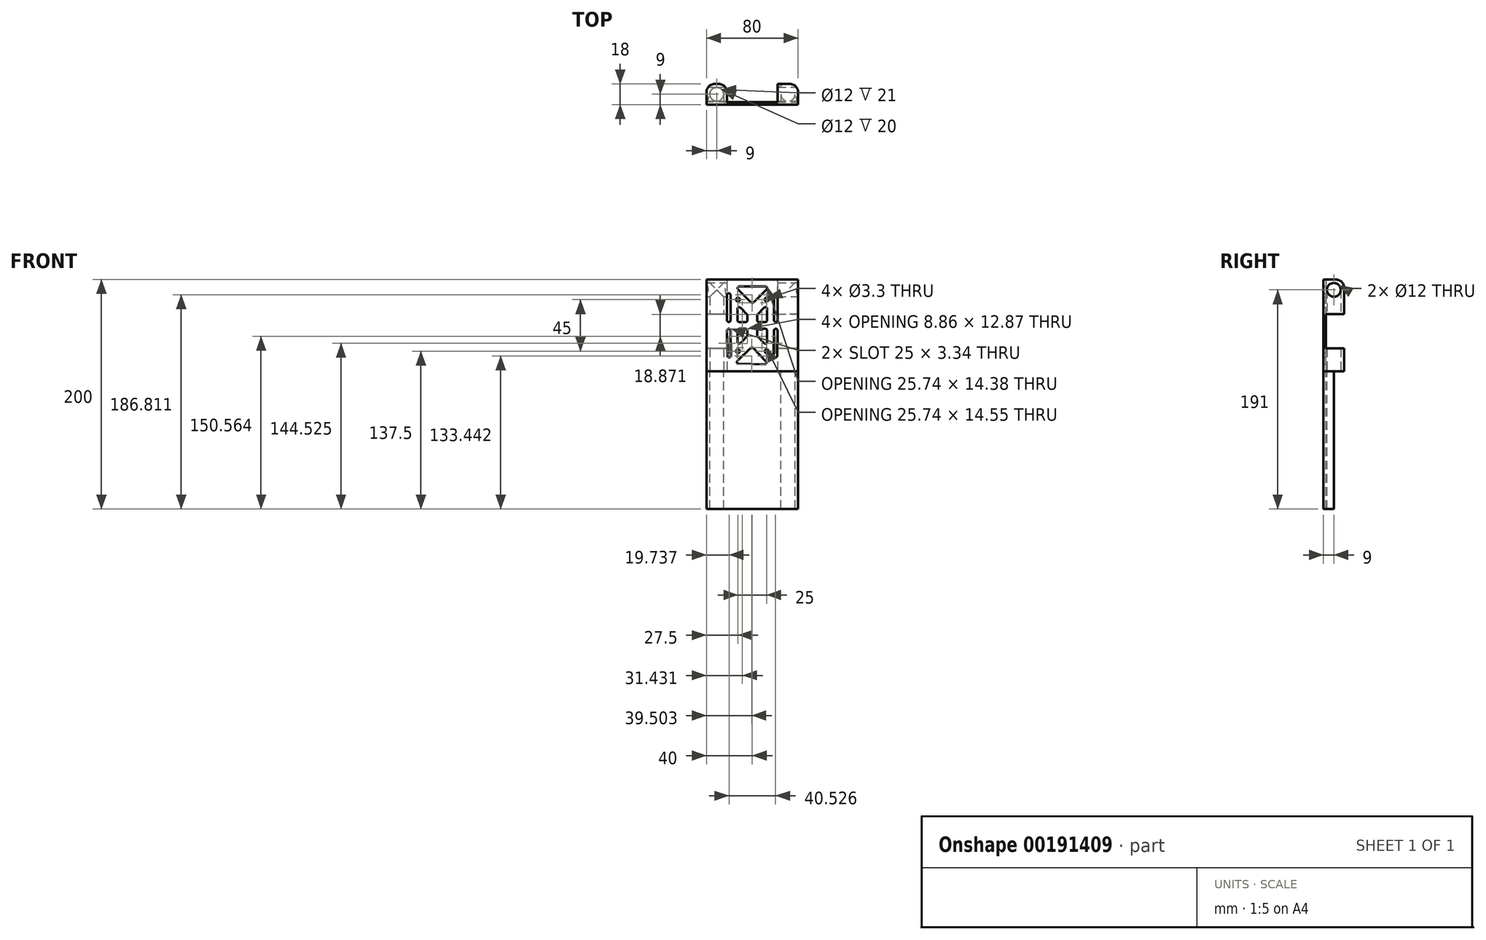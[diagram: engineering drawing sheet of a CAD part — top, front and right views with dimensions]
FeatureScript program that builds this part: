
annotation { "Feature Type Name" : "Feature", "Feature Type Description" : "" }
export const myFeature = defineFeature(function(context is Context, id is Id, definition is map)
    precondition{}
    {
        {
            var Q0;
            Q0=qCreatedBy(makeId("Top.planeOp"),FACE);
            var sketch = newSketch(context, id + "F0", { "sketchPlane" : qUnion([Q0])});
            skLineSegment(sketch, "E0.bottom", {"start": v(-40, 9) * mm, "end": v(40, 9) * mm});
            skLineSegment(sketch, "E0.top", {"start": v(-40, -9) * mm, "end": v(40, -9) * mm});
            skLineSegment(sketch, "E0.left", {"start": v(-40, 9) * mm, "end": v(-40, -9) * mm});
            skLineSegment(sketch, "E0.right", {"start": v(40, 9) * mm, "end": v(40, -9) * mm});
            skSolve(sketch);
        }
        {
            var Q0;
            Q0=qCreatedBy(makeId("Top.planeOp"),FACE);
            var sketch = newSketch(context, id + "F1", { "sketchPlane" : qUnion([Q0])});
            skCircle(sketch, "E1", {"center": v(-31, 0) * mm, "radius": 6 * mm});
            skCircle(sketch, "E2.MirrorC", {"center": v(31, 0) * mm, "radius": 6 * mm});
            skSolve(sketch);
        }
        {
            var Q0;
            Q0=makeQuery(id+"F0.imprint","IMPRINT",FACE,{"disambiguationData":[TD([[makeQuery(id+"F0.imprint","IMPRINT",EDGE,{"derivedFrom":sQuery(id+"F0.wireOp",EDGE,"E0.bottom")}),-1.0]])]});
            extrude(context, id + "F2", {"entities" : qUnion([Q0]), "depth" : 80 * mm});
        }
        {
            var Q0;
            Q0=makeQuery(id+"F2.opExtrude","SWEPT_FACE",FACE,{"disambiguationData":[OSD([sQuery(id+"F0.wireOp",EDGE,"E0.right")])]});
            var sketch = newSketch(context, id + "F3", { "sketchPlane" : qUnion([Q0])});
            skCircle(sketch, "E3", {"center": v(0, 71) * mm, "radius": 6 * mm});
            skSolve(sketch);
        }
        {
            var Q0;
            Q0 = qSketchRegion(id + "F3", true);
            extrude(context, id + "F4", {"entities" : qUnion([Q0]), "operationType" : NewBodyOperationType.REMOVE, "endBound" : BoundingType.UP_TO_NEXT, "oppositeDirection" : true, "depth" : 25 * mm});
        }
        {
            var Q0;
            Q0=makeQuery(id+"F1.imprint","IMPRINT",FACE,{"disambiguationData":[TD([[makeQuery(id+"F1.imprint","IMPRINT",EDGE,{"derivedFrom":sQuery(id+"F1.wireOp",EDGE,"E2.MirrorC")}),-1.0]])]});
            var Q1;
            Q1=makeQuery(id+"F1.imprint","IMPRINT",FACE,{"disambiguationData":[TD([[makeQuery(id+"F1.imprint","IMPRINT",EDGE,{"derivedFrom":sQuery(id+"F1.wireOp",EDGE,"E1")}),1.0]])]});
            extrude(context, id + "F5", {"entities" : qUnion([Q0, Q1]), "operationType" : NewBodyOperationType.REMOVE, "endBound" : BoundingType.UP_TO_NEXT, "depth" : 63.6 * mm});
        }
        {
            var Q0;
            Q0=makeQuery(id+"F2.opExtrude","SWEPT_FACE",FACE,{"disambiguationData":[OSD([sQuery(id+"F0.wireOp",EDGE,"E0.bottom")])]});
            var sketch = newSketch(context, id + "F6", { "sketchPlane" : qUnion([Q0])});
            skLineSegment(sketch, "E4.0", {"start": v(-22, 62) * mm, "end": v(-22, 0) * mm});
            skLineSegment(sketch, "E5", {"start": v(22, 0) * mm, "end": v(-22, 0) * mm});
            skLineSegment(sketch, "E6", {"start": v(-22, 62) * mm, "end": v(-22, 80) * mm});
            skLineSegment(sketch, "E7", {"start": v(-22, 80) * mm, "end": v(22, 80) * mm});
            skLineSegment(sketch, "E8", {"start": v(22, 80) * mm, "end": v(22, 0) * mm});
            skLineSegment(sketch, "E9.bottom", {"start": v(-22, 20) * mm, "end": v(-40, 20) * mm});
            skLineSegment(sketch, "E9.top", {"start": v(-22, 50) * mm, "end": v(-40, 50) * mm});
            skLineSegment(sketch, "E9.left", {"start": v(-22, 20) * mm, "end": v(-22, 50) * mm});
            skLineSegment(sketch, "E9.right", {"start": v(-40, 20) * mm, "end": v(-40, 50) * mm});
            skLineSegment(sketch, "E10.MirrorCS", {"start": v(40, 20) * mm, "end": v(40, 50) * mm});
            skLineSegment(sketch, "E11.MirrorCS", {"start": v(22, 50) * mm, "end": v(40, 50) * mm});
            skLineSegment(sketch, "E12.MirrorCS", {"start": v(22, 20) * mm, "end": v(22, 50) * mm});
            skLineSegment(sketch, "E13.MirrorCS", {"start": v(22, 20) * mm, "end": v(40, 20) * mm});
            skSolve(sketch);
        }
        {
            var Q0;
            Q0 = qSketchRegion(id + "F6", true);
            extrude(context, id + "F7", {"entities" : qUnion([Q0]), "operationType" : NewBodyOperationType.REMOVE, "oppositeDirection" : true, "depth" : 16 * mm});
        }
        {
            var Q0;
            Q0=makeQuery(id+"F2.opExtrude","SWEPT_FACE",FACE,{"disambiguationData":[OSD([sQuery(id+"F0.wireOp",EDGE,"E0.top")])]});
            cPlane(context, id + "F8", {"entities" : qUnion([Q0]), "cplaneType" : CPlaneType.OFFSET, "offset" : 0 * mm, "width" : 150 * mm, "height" : 150 * mm});
        }
        {
            var Q0;
            Q0=qCreatedBy(id+"F8.planeOp",FACE);
            var sketch = newSketch(context, id + "F9", { "sketchPlane" : qUnion([Q0])});
            skPoint(sketch, "E14", {"position": v(-12.5, 62.5) * mm});
            skPoint(sketch, "E15.MirrorP", {"position": v(12.5, 62.5) * mm});
            skPoint(sketch, "E16", {"position": v(-12.5, 17.5) * mm});
            skPoint(sketch, "E17.MirrorP", {"position": v(12.5, 17.5) * mm});
            skSolve(sketch);
        }
        {
            var Q0;
            Q0=sQuery(id+"F9.wireOp",VERTEX,"E15.MirrorP");
            var Q1;
            Q1=sQuery(id+"F9.wireOp",VERTEX,"E17.MirrorP");
            var Q2;
            Q2=sQuery(id+"F9.wireOp",VERTEX,"E16");
            var Q3;
            Q3=sQuery(id+"F9.wireOp",VERTEX,"E14");
            var Q4;
            Q4=makeQuery(id+"F2.opExtrude","SWEPT_BODY",BODY,{"disambiguationData":[OSD([sQuery(id+"F0.wireOp",EDGE,"E0.bottom"),sQuery(id+"F0.wireOp",EDGE,"E0.top"),sQuery(id+"F0.wireOp",EDGE,"E0.left"),sQuery(id+"F0.wireOp",EDGE,"E0.right")])]});
            hole(context, id + "F10", {"style" : HoleStyle.SIMPLE, "endStyle" : HoleEndStyle.THROUGH, "standardTappedOrClearance" : lookupTablePath({ "standard" : "ISO", "fit" : "Normal", "size" : "M3", "type" : "Clearance" }), "standardBlindInLast" : lookupTablePath({ "fit" : "Standard", "standard" : "ISO", "size" : "M3", "type" : "Clearance" }), "holeDiameter" : 3.3 * mm, "locations" : qUnion([Q0, Q1, Q2, Q3]), "scope" : qUnion([Q4]), "isTappedThrough" : true});
        }
        {
            var Q0;
            Q0=makeQuery(id+"F7.boolean.opBoolean","COPY",FACE,{"derivedFrom":makeQuery(id+"F7.opExtrude","CAP_FACE",FACE,{"disambiguationData":[OSD([sQuery(id+"F6.wireOp",EDGE,"E4.0"),sQuery(id+"F6.wireOp",EDGE,"E5"),sQuery(id+"F6.wireOp",EDGE,"E6"),sQuery(id+"F6.wireOp",EDGE,"E7"),sQuery(id+"F6.wireOp",EDGE,"E8")])],"isStart":false})});
            var sketch = newSketch(context, id + "F11", { "sketchPlane" : qUnion([Q0])});
            skLineSegment(sketch, "E18", {"start": v(-11.38, 74) * mm, "end": v(11.38, 74) * mm});
            skLineSegment(sketch, "E19", {"start": v(12.44, 71.44) * mm, "end": v(1.06, 60.06) * mm});
            skLineSegment(sketch, "E20", {"start": v(-1.06, 60.06) * mm, "end": v(-12.44, 71.44) * mm});
            skLineSegment(sketch, "E21.bottom", {"start": v(-20.5, 68) * mm, "end": v(-20.5, 68) * mm});
            skLineSegment(sketch, "E21.top", {"start": v(-20.5, 43) * mm, "end": v(-20.5, 43) * mm});
            skLineSegment(sketch, "E21.left", {"start": v(-22, 66.5) * mm, "end": v(-22, 44.5) * mm});
            skLineSegment(sketch, "E21.right", {"start": v(-19, 66.5) * mm, "end": v(-19, 44.5) * mm});
            skPoint(sketch, "E22.visualSharp", {"position": v(-22, 68) * mm});
            skArc(sketch, "E22.filletArc", {"start": v(-20.5, 68) * mm, "mid": v(-21.56, 67.56) * mm, "end": v(-22, 66.5) * mm});
            skPoint(sketch, "E23.visualSharp", {"position": v(-19, 68) * mm});
            skArc(sketch, "E23.filletArc", {"start": v(-19, 66.5) * mm, "mid": v(-19.44, 67.56) * mm, "end": v(-20.5, 68) * mm});
            skPoint(sketch, "E24.visualSharp", {"position": v(-22, 43) * mm});
            skArc(sketch, "E24.filletArc", {"start": v(-22, 44.5) * mm, "mid": v(-21.56, 43.44) * mm, "end": v(-20.5, 43) * mm});
            skPoint(sketch, "E25.visualSharp", {"position": v(-19, 43) * mm});
            skArc(sketch, "E25.filletArc", {"start": v(-20.5, 43) * mm, "mid": v(-19.44, 43.44) * mm, "end": v(-19, 44.5) * mm});
            skPoint(sketch, "E26.visualSharp", {"position": v(0, 59) * mm});
            skArc(sketch, "E26.filletArc", {"start": v(-1.06, 60.06) * mm, "mid": v(0, 59.62) * mm, "end": v(1.06, 60.06) * mm});
            skPoint(sketch, "E27.visualSharp", {"position": v(-15, 74) * mm});
            skArc(sketch, "E27.filletArc", {"start": v(-11.38, 74) * mm, "mid": v(-12.76, 73.07) * mm, "end": v(-12.44, 71.44) * mm});
            skPoint(sketch, "E28.visualSharp", {"position": v(15, 74) * mm});
            skArc(sketch, "E28.filletArc", {"start": v(12.44, 71.44) * mm, "mid": v(12.76, 73.07) * mm, "end": v(11.38, 74) * mm});
            skArc(sketch, "E29.MirrorCS", {"start": v(-20.45, 37.02) * mm, "mid": v(-19.39, 36.6) * mm, "end": v(-18.93, 35.55) * mm});
            skArc(sketch, "E30.MirrorCS", {"start": v(-21.93, 35.5) * mm, "mid": v(-21.5, 36.57) * mm, "end": v(-20.45, 37.02) * mm});
            skArc(sketch, "E31.MirrorCS", {"start": v(-20.07, 12.03) * mm, "mid": v(-21.14, 12.45) * mm, "end": v(-21.6, 13.5) * mm});
            skArc(sketch, "E32.MirrorCS", {"start": v(-18.6, 13.55) * mm, "mid": v(-19.02, 12.48) * mm, "end": v(-20.07, 12.03) * mm});
            skArc(sketch, "E33.MirrorCS", {"start": v(-0.76, 20.26) * mm, "mid": v(0.3, 20.72) * mm, "end": v(1.36, 20.3) * mm});
            skLineSegment(sketch, "E34.MirrorCS", {"start": v(-20.45, 37.02) * mm, "end": v(-20.45, 37.02) * mm});
            skPoint(sketch, "E35.MirrorP", {"position": v(-18.95, 37.05) * mm});
            skArc(sketch, "E36.MirrorCS", {"start": v(-10.86, 6.17) * mm, "mid": v(-12.26, 7.07) * mm, "end": v(-11.96, 8.71) * mm});
            skArc(sketch, "E37.MirrorCS", {"start": v(12.92, 9.1) * mm, "mid": v(13.27, 7.46) * mm, "end": v(11.9, 6.51) * mm});
            skPoint(sketch, "E38.MirrorP", {"position": v(15.52, 6.57) * mm});
            skPoint(sketch, "E39.MirrorP", {"position": v(0.29, 21.34) * mm});
            skPoint(sketch, "E40.MirrorP", {"position": v(-21.95, 37) * mm});
            skLineSegment(sketch, "E41.MirrorCS", {"start": v(-10.86, 6.17) * mm, "end": v(11.9, 6.51) * mm});
            skLineSegment(sketch, "E42.MirrorCS", {"start": v(-20.07, 12.03) * mm, "end": v(-20.07, 12.03) * mm});
            skPoint(sketch, "E43.MirrorP", {"position": v(-14.48, 6.11) * mm});
            skPoint(sketch, "E44.MirrorP", {"position": v(-18.57, 12.05) * mm});
            skLineSegment(sketch, "E45.MirrorCS", {"start": v(-21.6, 13.5) * mm, "end": v(-21.93, 35.5) * mm});
            skPoint(sketch, "E46.MirrorP", {"position": v(-21.57, 12) * mm});
            skLineSegment(sketch, "E47.MirrorCS", {"start": v(12.92, 9.1) * mm, "end": v(1.36, 20.3) * mm});
            skLineSegment(sketch, "E48.MirrorCS", {"start": v(-18.6, 13.55) * mm, "end": v(-18.93, 35.55) * mm});
            skLineSegment(sketch, "E49.MirrorCS", {"start": v(-0.76, 20.26) * mm, "end": v(-11.96, 8.71) * mm});
            skArc(sketch, "E50.MirrorCS", {"start": v(21.93, 35.5) * mm, "mid": v(21.5, 36.57) * mm, "end": v(20.45, 37.02) * mm});
            skArc(sketch, "E51.MirrorCS", {"start": v(19, 66.5) * mm, "mid": v(19.44, 67.56) * mm, "end": v(20.5, 68) * mm});
            skArc(sketch, "E52.MirrorCS", {"start": v(22, 44.5) * mm, "mid": v(21.56, 43.44) * mm, "end": v(20.5, 43) * mm});
            skArc(sketch, "E53.MirrorCS", {"start": v(20.5, 43) * mm, "mid": v(19.44, 43.44) * mm, "end": v(19, 44.5) * mm});
            skArc(sketch, "E54.MirrorCS", {"start": v(18.6, 13.55) * mm, "mid": v(19.02, 12.48) * mm, "end": v(20.07, 12.03) * mm});
            skArc(sketch, "E55.MirrorCS", {"start": v(20.07, 12.03) * mm, "mid": v(21.14, 12.45) * mm, "end": v(21.6, 13.5) * mm});
            skArc(sketch, "E56.MirrorCS", {"start": v(20.5, 68) * mm, "mid": v(21.56, 67.56) * mm, "end": v(22, 66.5) * mm});
            skArc(sketch, "E57.MirrorCS", {"start": v(20.45, 37.02) * mm, "mid": v(19.39, 36.6) * mm, "end": v(18.93, 35.55) * mm});
            skPoint(sketch, "E58.MirrorP", {"position": v(18.95, 37.05) * mm});
            skPoint(sketch, "E59.MirrorP", {"position": v(19, 43) * mm});
            skLineSegment(sketch, "E60.MirrorCS", {"start": v(21.6, 13.5) * mm, "end": v(21.93, 35.5) * mm});
            skPoint(sketch, "E61.MirrorP", {"position": v(21.57, 12) * mm});
            skLineSegment(sketch, "E62.MirrorCS", {"start": v(22, 66.5) * mm, "end": v(22, 44.5) * mm});
            skPoint(sketch, "E63.MirrorP", {"position": v(21.95, 37) * mm});
            skLineSegment(sketch, "E64.MirrorCS", {"start": v(19, 66.5) * mm, "end": v(19, 44.5) * mm});
            skPoint(sketch, "E65.MirrorP", {"position": v(18.57, 12.05) * mm});
            skLineSegment(sketch, "E66.MirrorCS", {"start": v(20.45, 37.02) * mm, "end": v(20.45, 37.02) * mm});
            skLineSegment(sketch, "E67.MirrorCS", {"start": v(18.6, 13.55) * mm, "end": v(18.93, 35.55) * mm});
            skPoint(sketch, "E68.MirrorP", {"position": v(22, 43) * mm});
            skPoint(sketch, "E69.MirrorP", {"position": v(19, 68) * mm});
            skLineSegment(sketch, "E70.MirrorCS", {"start": v(20.5, 43) * mm, "end": v(20.5, 43) * mm});
            skLineSegment(sketch, "E71.MirrorCS", {"start": v(20.07, 12.03) * mm, "end": v(20.07, 12.03) * mm});
            skLineSegment(sketch, "E72.MirrorCS", {"start": v(20.5, 68) * mm, "end": v(20.5, 68) * mm});
            skPoint(sketch, "E73.MirrorP", {"position": v(22, 68) * mm});
            skLineSegment(sketch, "E74", {"start": v(-13, 54.38) * mm, "end": v(-13, 44.5) * mm});
            skLineSegment(sketch, "E75", {"start": v(-11.5, 43) * mm, "end": v(-5.64, 43) * mm});
            skLineSegment(sketch, "E76", {"start": v(-4.14, 44.5) * mm, "end": v(-4.14, 48.52) * mm});
            skLineSegment(sketch, "E77", {"start": v(-4.58, 49.58) * mm, "end": v(-10.44, 55.44) * mm});
            skPoint(sketch, "E78.visualSharp", {"position": v(-13, 58) * mm});
            skArc(sketch, "E78.filletArc", {"start": v(-10.44, 55.44) * mm, "mid": v(-12.07, 55.76) * mm, "end": v(-13, 54.38) * mm});
            skPoint(sketch, "E79.visualSharp", {"position": v(-4.14, 49.14) * mm});
            skArc(sketch, "E79.filletArc", {"start": v(-4.14, 48.52) * mm, "mid": v(-4.25, 49.1) * mm, "end": v(-4.58, 49.58) * mm});
            skPoint(sketch, "E80.visualSharp", {"position": v(-4.14, 43) * mm});
            skArc(sketch, "E80.filletArc", {"start": v(-5.64, 43) * mm, "mid": v(-4.58, 43.44) * mm, "end": v(-4.14, 44.5) * mm});
            skPoint(sketch, "E81.visualSharp", {"position": v(-13, 43) * mm});
            skArc(sketch, "E81.filletArc", {"start": v(-13, 44.5) * mm, "mid": v(-12.56, 43.44) * mm, "end": v(-11.5, 43) * mm});
            skArc(sketch, "E82.MirrorCS", {"start": v(-4.14, 31.48) * mm, "mid": v(-4.25, 30.9) * mm, "end": v(-4.58, 30.42) * mm});
            skLineSegment(sketch, "E83.MirrorCS", {"start": v(-13, 25.62) * mm, "end": v(-13, 35.5) * mm});
            skArc(sketch, "E84.MirrorCS", {"start": v(-5.64, 37) * mm, "mid": v(-4.58, 36.56) * mm, "end": v(-4.14, 35.5) * mm});
            skArc(sketch, "E85.MirrorCS", {"start": v(-13, 35.5) * mm, "mid": v(-12.56, 36.56) * mm, "end": v(-11.5, 37) * mm});
            skLineSegment(sketch, "E86.MirrorCS", {"start": v(-11.5, 37) * mm, "end": v(-5.64, 37) * mm});
            skArc(sketch, "E87.MirrorCS", {"start": v(-10.44, 24.56) * mm, "mid": v(-12.07, 24.24) * mm, "end": v(-13, 25.62) * mm});
            skLineSegment(sketch, "E88.MirrorCS", {"start": v(-4.14, 35.5) * mm, "end": v(-4.14, 31.48) * mm});
            skLineSegment(sketch, "E89.MirrorCS", {"start": v(-4.58, 30.42) * mm, "end": v(-10.44, 24.56) * mm});
            skPoint(sketch, "E90.MirrorP", {"position": v(-4.14, 33.36) * mm});
            skArc(sketch, "E91.MirrorCS", {"start": v(4.14, 48.52) * mm, "mid": v(4.25, 49.1) * mm, "end": v(4.58, 49.58) * mm});
            skArc(sketch, "E92.MirrorCS", {"start": v(4.14, 31.48) * mm, "mid": v(4.25, 30.9) * mm, "end": v(4.58, 30.42) * mm});
            skArc(sketch, "E93.MirrorCS", {"start": v(5.64, 43) * mm, "mid": v(4.58, 43.44) * mm, "end": v(4.14, 44.5) * mm});
            skArc(sketch, "E94.MirrorCS", {"start": v(13, 44.5) * mm, "mid": v(12.56, 43.44) * mm, "end": v(11.5, 43) * mm});
            skPoint(sketch, "E95.MirrorP", {"position": v(13, 58) * mm});
            skLineSegment(sketch, "E96.MirrorCS", {"start": v(13, 25.62) * mm, "end": v(13, 35.5) * mm});
            skLineSegment(sketch, "E97.MirrorCS", {"start": v(11.5, 37) * mm, "end": v(5.64, 37) * mm});
            skLineSegment(sketch, "E98.MirrorCS", {"start": v(13, 54.38) * mm, "end": v(13, 44.5) * mm});
            skLineSegment(sketch, "E99.MirrorCS", {"start": v(4.58, 49.58) * mm, "end": v(10.44, 55.44) * mm});
            skArc(sketch, "E100.MirrorCS", {"start": v(10.44, 24.56) * mm, "mid": v(12.07, 24.24) * mm, "end": v(13, 25.62) * mm});
            skPoint(sketch, "E101.MirrorP", {"position": v(4.14, 33.36) * mm});
            skPoint(sketch, "E102.MirrorP", {"position": v(4.14, 49.14) * mm});
            skLineSegment(sketch, "E103.MirrorCS", {"start": v(4.14, 35.5) * mm, "end": v(4.14, 31.48) * mm});
            skArc(sketch, "E104.MirrorCS", {"start": v(5.64, 37) * mm, "mid": v(4.58, 36.56) * mm, "end": v(4.14, 35.5) * mm});
            skArc(sketch, "E105.MirrorCS", {"start": v(13, 35.5) * mm, "mid": v(12.56, 36.56) * mm, "end": v(11.5, 37) * mm});
            skArc(sketch, "E106.MirrorCS", {"start": v(10.44, 55.44) * mm, "mid": v(12.07, 55.76) * mm, "end": v(13, 54.38) * mm});
            skPoint(sketch, "E107.MirrorP", {"position": v(4.14, 43) * mm});
            skLineSegment(sketch, "E108.MirrorCS", {"start": v(4.14, 44.5) * mm, "end": v(4.14, 48.52) * mm});
            skLineSegment(sketch, "E109.MirrorCS", {"start": v(11.5, 43) * mm, "end": v(5.64, 43) * mm});
            skLineSegment(sketch, "E110.MirrorCS", {"start": v(4.58, 30.42) * mm, "end": v(10.44, 24.56) * mm});
            skPoint(sketch, "E111.MirrorP", {"position": v(13, 43) * mm});
            skLineSegment(sketch, "E112", {"start": v(-22, 40) * mm, "end": v(22, 40) * mm, "construction": true});
            skSolve(sketch);
        }
        {
            var Q0;
            Q0=makeQuery(id+"F2.opExtrude","SWEPT_EDGE",EDGE,{"disambiguationData":[OSD([sQuery(id+"F0.wireOp",EDGE,"E0.bottom"),sQuery(id+"F0.wireOp",EDGE,"E0.left")])]});
            var Q1;
            Q1=makeQuery(id+"F2.opExtrude","SWEPT_EDGE",EDGE,{"disambiguationData":[OSD([sQuery(id+"F0.wireOp",EDGE,"E0.bottom"),sQuery(id+"F0.wireOp",EDGE,"E0.right")])]});
            var Q2;
            Q2=makeQuery(id+"F2.opExtrude","CAP_EDGE",EDGE,{"disambiguationData":[OSD([sQuery(id+"F0.wireOp",EDGE,"E0.bottom")])],"isStart":false});
            var Q3;
            Q3=makeQuery(id+"F7.boolean.opBoolean","COPY",EDGE,{"derivedFrom":makeQuery(id+"F7.opExtrude","CAP_EDGE",EDGE,{"disambiguationData":[OSD([sQuery(id+"F6.wireOp",EDGE,"E4.2")])],"isStart":true})});
            var Q4;
            Q4=makeQuery(id+"F7.boolean.opBoolean","COPY",EDGE,{"derivedFrom":makeQuery(id+"F7.opExtrude","CAP_EDGE",EDGE,{"disambiguationData":[OSD([sQuery(id+"F6.wireOp",EDGE,"E4.0")])],"isStart":true})});
            var Q5;
            Q5=makeQuery(id+"F7.boolean.opBoolean","COPY",EDGE,{"derivedFrom":makeQuery(id+"F7.opExtrude","CAP_EDGE",EDGE,{"disambiguationData":[OSD([sQuery(id+"F6.wireOp",EDGE,"E4.1")])],"isStart":true})});
            var Q6;
            Q6=makeQuery(id+"F7.boolean.opBoolean","COPY",EDGE,{"derivedFrom":makeQuery(id+"F7.opExtrude","CAP_EDGE",EDGE,{"disambiguationData":[OSD([sQuery(id+"F6.wireOp",EDGE,"E8")])],"isStart":true})});
            fillet(context, id + "F12", {"entities" : qUnion([Q0, Q1, Q2, Q3, Q4, Q5, Q6]), "radius" : 7.4 * mm, "tangentPropagation" : true, "allowEdgeOverflow" : false});
        }
        {
            var Q0;
            Q0 = qSketchRegion(id + "F11", true);
            extrude(context, id + "F13", {"entities" : qUnion([Q0]), "operationType" : NewBodyOperationType.REMOVE, "endBound" : BoundingType.UP_TO_NEXT, "oppositeDirection" : true, "depth" : 25 * mm});
        }
        {
            var Q0;
            Q0=makeQuery(id+"F2.opExtrude","CAP_FACE",FACE,{"disambiguationData":[OSD([sQuery(id+"F0.wireOp",EDGE,"E0.bottom"),sQuery(id+"F0.wireOp",EDGE,"E0.top"),sQuery(id+"F0.wireOp",EDGE,"E0.left"),sQuery(id+"F0.wireOp",EDGE,"E0.right")])],"isStart":true});
            var sketch = newSketch(context, id + "F14", { "sketchPlane" : qUnion([Q0])});
            skLineSegment(sketch, "E113", {"start": v(-25, 0) * mm, "end": v(-25, 7) * mm});
            skLineSegment(sketch, "E114", {"start": v(-25, 7) * mm, "end": v(-22, 7) * mm});
            skLineSegment(sketch, "E115", {"start": v(-22, 7) * mm, "end": v(22, 7) * mm});
            skLineSegment(sketch, "E116", {"start": v(25, 0) * mm, "end": v(25, 7) * mm});
            skLineSegment(sketch, "E117", {"start": v(25, 7) * mm, "end": v(22, 7) * mm});
            skLineSegment(sketch, "E118", {"start": v(-40, 9) * mm, "end": v(40, 9) * mm});
            skLineSegment(sketch, "E119", {"start": v(40, 9) * mm, "end": v(37.27, 0) * mm});
            skLineSegment(sketch, "E120", {"start": v(-40, 9) * mm, "end": v(-37, 0) * mm});
            skArc(sketch, "E121", {"start": v(-25, 0) * mm, "mid": v(-31, 6) * mm, "end": v(-37, 0) * mm});
            skArc(sketch, "E122", {"start": v(37.27, 0) * mm, "mid": v(31.13, 6.13) * mm, "end": v(25, 0) * mm});
            skSolve(sketch);
        }
        {
            var Q0;
            Q0 = qSketchRegion(id + "F14", true);
            extrude(context, id + "F15", {"entities" : qUnion([Q0]), "offsetDistance" : 25 * mm, "depth" : 120 * mm});
        }
    });
